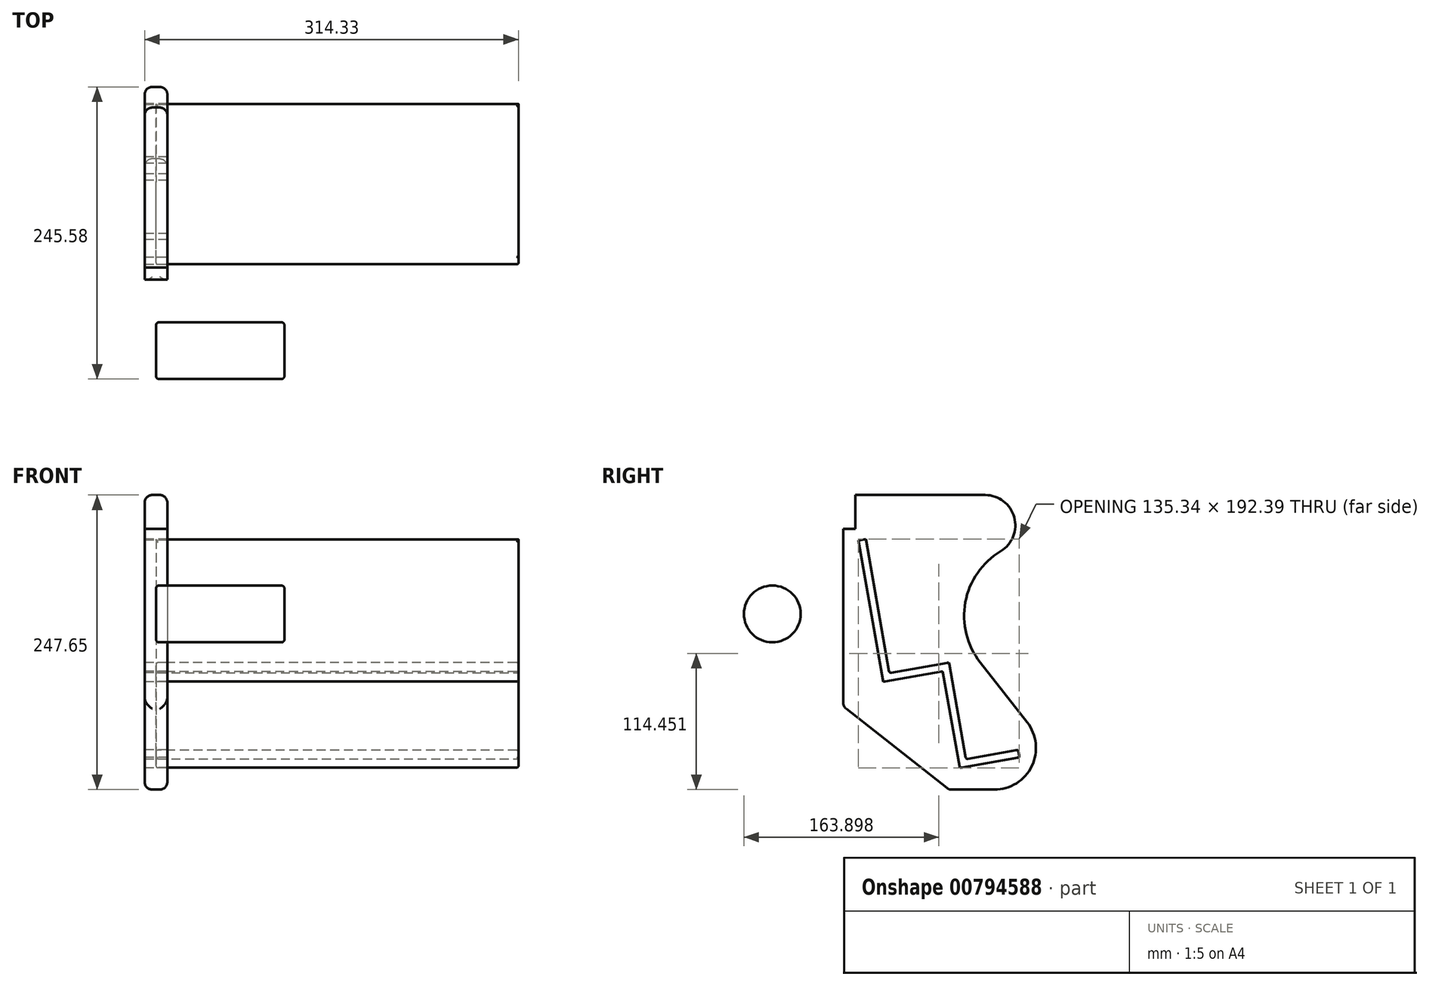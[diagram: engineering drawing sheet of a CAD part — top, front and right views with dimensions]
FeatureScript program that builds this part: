
annotation { "Feature Type Name" : "Feature", "Feature Type Description" : "" }
export const myFeature = defineFeature(function(context is Context, id is Id, definition is map)
    precondition{}
    {
        {
            var Q0;
            Q0=qCreatedBy(makeId("Right.planeOp"),FACE);
            var sketch = newSketch(context, id + "F0", { "sketchPlane" : qUnion([Q0])});
            skLineSegment(sketch, "E0", {"start": v(-356.25, 1.24) * mm, "end": v(-336.4, -111.33) * mm});
            skLineSegment(sketch, "E1", {"start": v(-350, 2.34) * mm, "end": v(-330.15, -110.23) * mm});
            skLineSegment(sketch, "E2", {"start": v(-356.25, 1.24) * mm, "end": v(-350, 2.34) * mm});
            skLineSegment(sketch, "E3.trimOffspring", {"start": v(-336.4, -111.33) * mm, "end": v(-330.15, -110.23) * mm});
            skLineSegment(sketch, "E4", {"start": v(-336.4, -111.33) * mm, "end": v(-286.38, -102.5) * mm});
            skLineSegment(sketch, "E5", {"start": v(-286.38, -102.5) * mm, "end": v(-285.27, -108.76) * mm});
            skLineSegment(sketch, "E6", {"start": v(-336.4, -111.33) * mm, "end": v(-335.3, -117.58) * mm});
            skLineSegment(sketch, "E7", {"start": v(-335.3, -117.58) * mm, "end": v(-285.27, -108.76) * mm});
            skLineSegment(sketch, "E8", {"start": v(-286.38, -102.5) * mm, "end": v(-280.12, -101.4) * mm});
            skLineSegment(sketch, "E9", {"start": v(-280.12, -101.4) * mm, "end": v(-265.79, -182.7) * mm});
            skLineSegment(sketch, "E10", {"start": v(-265.79, -182.7) * mm, "end": v(-272.04, -183.8) * mm});
            skLineSegment(sketch, "E11", {"start": v(-272.04, -183.8) * mm, "end": v(-286.38, -102.5) * mm});
            skLineSegment(sketch, "E12", {"start": v(-272.04, -183.8) * mm, "end": v(-222.01, -174.98) * mm});
            skLineSegment(sketch, "E13", {"start": v(-222.01, -174.98) * mm, "end": v(-220.91, -181.23) * mm});
            skLineSegment(sketch, "E14", {"start": v(-220.91, -181.23) * mm, "end": v(-270.94, -190.06) * mm});
            skLineSegment(sketch, "E15", {"start": v(-270.94, -190.06) * mm, "end": v(-272.04, -183.8) * mm});
            skLineSegment(sketch, "E16", {"start": v(-358.8, 39.34) * mm, "end": v(-249.64, 39.34) * mm});
            skLineSegment(sketch, "E17", {"start": v(-368.95, 10.89) * mm, "end": v(-368.95, -138.46) * mm});
            skLineSegment(sketch, "E18", {"start": v(-280.05, -208.31) * mm, "end": v(-241.95, -208.31) * mm});
            skArc(sketch, "E19", {"start": v(-236.56, -7.84) * mm, "mid": v(-266.3, -50.79) * mm, "end": v(-253.77, -101.5) * mm});
            skArc(sketch, "E20", {"start": v(-241.95, -208.31) * mm, "mid": v(-210.43, -188.58) * mm, "end": v(-214.4, -151.6) * mm});
            skLineSegment(sketch, "E21", {"start": v(-253.77, -101.5) * mm, "end": v(-214.4, -151.6) * mm});
            skLineSegment(sketch, "E22", {"start": v(-280.05, -208.31) * mm, "end": v(-368.95, -138.46) * mm});
            skArc(sketch, "E23", {"start": v(-236.56, -7.84) * mm, "mid": v(-225.17, 20.72) * mm, "end": v(-249.64, 39.34) * mm});
            skPoint(sketch, "E23.centerSnap0", {"position": v(-249.64, -18.27) * mm});
            skLineSegment(sketch, "E24", {"start": v(-358.8, 39.34) * mm, "end": v(-358.8, 10.89) * mm});
            skLineSegment(sketch, "E25", {"start": v(-358.8, 10.89) * mm, "end": v(-368.95, 10.89) * mm});
            skSolve(sketch);
        }
        {
            var Q0;
            {var subQ0=sQuery(id+"F0.wireOp",EDGE,"E0");Q0=makeQuery(id+"F0.imprint","IMPRINT",FACE,{"disambiguationData":[TD([[makeQuery(id+"F0.imprint","IMPRINT",EDGE,{"derivedFrom":subQ0}),1.0]])]});}
            var Q1;
            {var subQ1=sQuery(id+"F0.wireOp",EDGE,"E6");Q1=makeQuery(id+"F0.imprint","IMPRINT",FACE,{"disambiguationData":[TD([[makeQuery(id+"F0.imprint","IMPRINT",EDGE,{"derivedFrom":subQ1}),1.0]])]});}
            var Q2;
            {var subQ1=sQuery(id+"F0.wireOp",EDGE,"E8");Q2=makeQuery(id+"F0.imprint","IMPRINT",FACE,{"disambiguationData":[TD([[makeQuery(id+"F0.imprint","IMPRINT",EDGE,{"derivedFrom":subQ1}),-1.0]])]});}
            var Q3;
            {var subQ0=sQuery(id+"F0.wireOp",EDGE,"E13");Q3=makeQuery(id+"F0.imprint","IMPRINT",FACE,{"disambiguationData":[TD([[makeQuery(id+"F0.imprint","IMPRINT",EDGE,{"derivedFrom":subQ0}),-1.0]])]});}
            extrude(context, id + "F1", {"entities" : qUnion([Q0, Q1, Q2, Q3]), "depth" : 304.8 * mm, "offsetDistance" : 25.4 * mm});
        }
        {
            var Q0;
            Q0 = qSketchRegion(id + "F0", true);
            extrude(context, id + "F2", {"entities" : qUnion([Q0]), "depth" : 19.05 * mm, "offsetDistance" : 25.4 * mm, "symmetric" : true});
        }
        {
            var Q0;
            Q0=qCreatedBy(makeId("Right.planeOp"),FACE);
            var sketch = newSketch(context, id + "F3", { "sketchPlane" : qUnion([Q0])});
            skCircle(sketch, "E26", {"center": v(-428.6, -60.62) * mm, "radius": 23.88 * mm});
            skSolve(sketch);
        }
        {
            var Q0;
            Q0 = qSketchRegion(id + "F3", true);
            extrude(context, id + "F4", {"entities" : qUnion([Q0]), "depth" : 107.95 * mm, "offsetDistance" : 25.4 * mm});
        }
        {
            var Q0;
            Q0=makeQuery(id+"F4.opExtrude","CAP_FACE",FACE,{"disambiguationData":[OSD([sQuery(id+"F3.wireOp",EDGE,"E26")])],"isStart":false});
            var Q1;
            Q1=makeQuery(id+"F4.opExtrude","CAP_FACE",FACE,{"disambiguationData":[OSD([sQuery(id+"F3.wireOp",EDGE,"E26")])],"isStart":true});
            fillet(context, id + "F5", {"entities" : qUnion([Q0, Q1]), "radius" : 2.54 * mm, "tangentPropagation" : true, "allowEdgeOverflow" : false});
        }
        {
            var Q0;
            Q0=makeQuery(id+"F2.opExtrude","SWEPT_FACE",FACE,{"disambiguationData":[OSD([sQuery(id+"F0.wireOp",EDGE,"E22")])]});
            var Q1;
            Q1=makeQuery(id+"F2.opExtrude","SWEPT_FACE",FACE,{"disambiguationData":[OSD([sQuery(id+"F0.wireOp",EDGE,"E18")])]});
            fillet(context, id + "F6", {"entities" : qUnion([Q0, Q1]), "radius" : 6.35 * mm, "tangentPropagation" : true, "allowEdgeOverflow" : false});
        }
        {
            var Q0;
            Q0=makeQuery(id+"F1.opExtrude","SWEPT_FACE",FACE,{"disambiguationData":[OSD([sQuery(id+"F0.wireOp",EDGE,"E1")])]});
            var Q1;
            Q1=makeQuery(id+"F1.opExtrude","SWEPT_FACE",FACE,{"disambiguationData":[OSD([sQuery(id+"F0.wireOp",EDGE,"E4"),sQuery(id+"F0.wireOp",EDGE,"E8")])]});
            var Q2;
            Q2=makeQuery(id+"F1.opExtrude","SWEPT_FACE",FACE,{"disambiguationData":[OSD([sQuery(id+"F0.wireOp",EDGE,"E9")])]});
            var Q3;
            Q3=makeQuery(id+"F1.opExtrude","SWEPT_FACE",FACE,{"disambiguationData":[OSD([sQuery(id+"F0.wireOp",EDGE,"E12")])]});
            var Q4;
            Q4=makeQuery(id+"F1.opExtrude","SWEPT_FACE",FACE,{"disambiguationData":[OSD([sQuery(id+"F0.wireOp",EDGE,"E14")])]});
            var Q5;
            Q5=makeQuery(id+"F1.opExtrude","SWEPT_FACE",FACE,{"disambiguationData":[OSD([sQuery(id+"F0.wireOp",EDGE,"E11"),sQuery(id+"F0.wireOp",EDGE,"E15")])]});
            var Q6;
            Q6=makeQuery(id+"F1.opExtrude","SWEPT_FACE",FACE,{"disambiguationData":[OSD([sQuery(id+"F0.wireOp",EDGE,"E7")])]});
            var Q7;
            Q7=makeQuery(id+"F1.opExtrude","SWEPT_FACE",FACE,{"disambiguationData":[OSD([sQuery(id+"F0.wireOp",EDGE,"E0"),sQuery(id+"F0.wireOp",EDGE,"E6")])]});
            fillet(context, id + "F7", {"entities" : qUnion([Q0, Q1, Q2, Q3, Q4, Q5, Q6, Q7]), "radius" : 1.52 * mm, "tangentPropagation" : true, "allowEdgeOverflow" : false});
        }
    });
